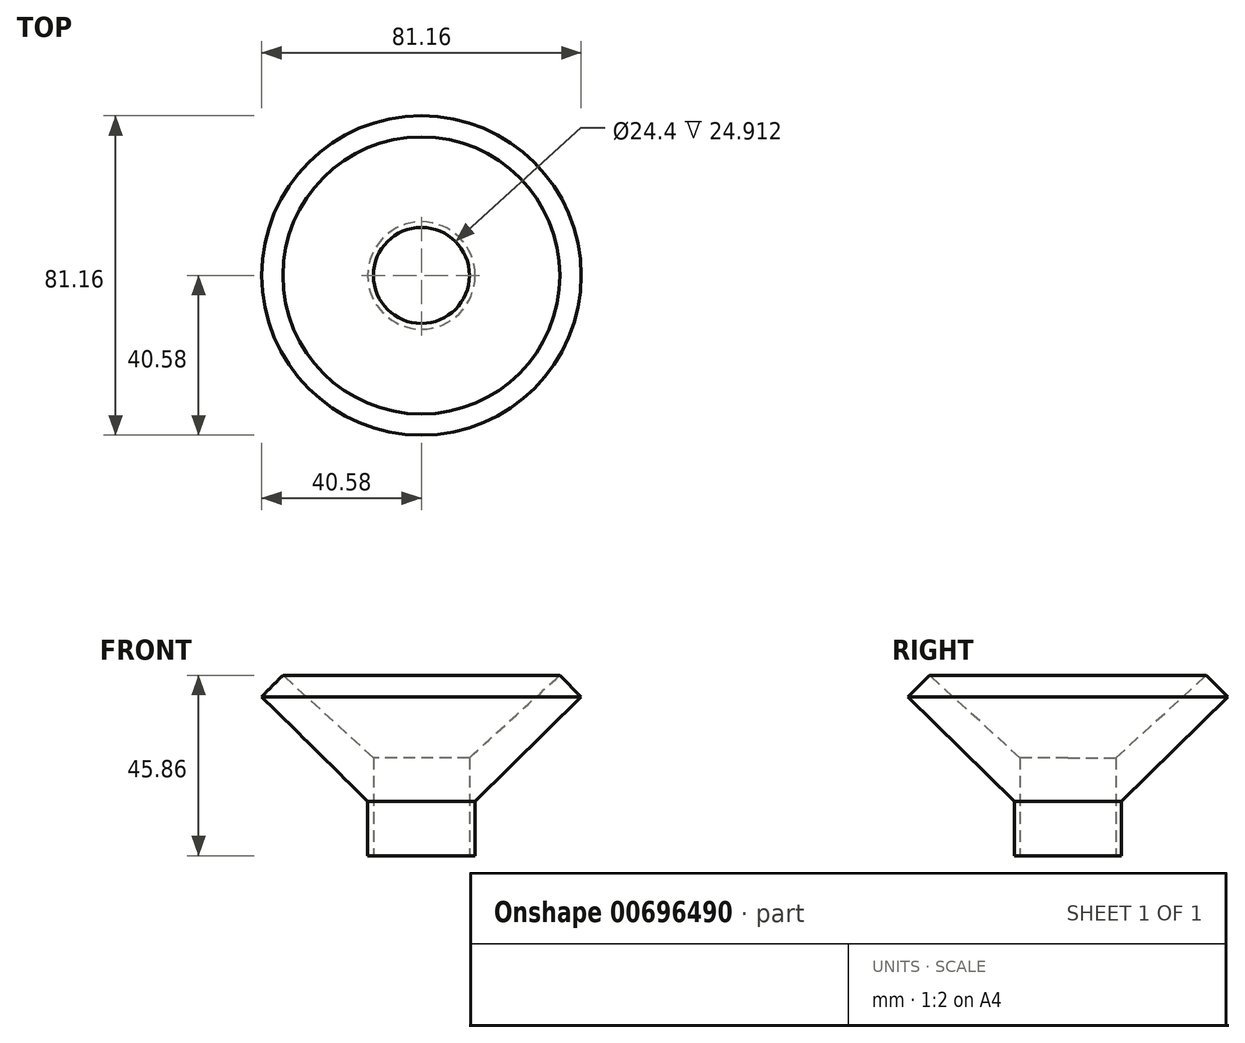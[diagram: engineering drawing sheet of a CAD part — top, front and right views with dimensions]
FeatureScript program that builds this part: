
annotation { "Feature Type Name" : "Feature", "Feature Type Description" : "" }
export const myFeature = defineFeature(function(context is Context, id is Id, definition is map)
    precondition{}
    {
        {
            var Q0;
            Q0=qCreatedBy(makeId("Front.planeOp"),FACE);
            var sketch = newSketch(context, id + "F0", { "sketchPlane" : qUnion([Q0])});
            skLineSegment(sketch, "E0.bottom", {"start": v(0, 0) * mm, "end": v(13.64, 0) * mm});
            skLineSegment(sketch, "E0.top", {"start": v(0, 13.8) * mm, "end": v(13.64, 13.8) * mm});
            skLineSegment(sketch, "E0.left", {"start": v(0, 0) * mm, "end": v(0, 13.8) * mm});
            skLineSegment(sketch, "E0.right", {"start": v(13.64, 0) * mm, "end": v(13.64, 13.8) * mm});
            skLineSegment(sketch, "E1", {"start": v(13.64, 13.8) * mm, "end": v(40.58, 40.42) * mm});
            skLineSegment(sketch, "E2", {"start": v(40.58, 40.42) * mm, "end": v(35.2, 45.86) * mm});
            skLineSegment(sketch, "E3", {"start": v(35.2, 45.86) * mm, "end": v(0, 13.8) * mm});
            skSolve(sketch);
        }
        {
            var Q0;
            Q0 = qSketchRegion(id + "F0", true);
            var Q1;
            Q1=sQuery(id+"F0.wireOp",EDGE,"E0.left");
            revolve(context, id + "F1", {"surfaceOperationType" : NewSurfaceOperationType.NEW, "entities" : qUnion([Q0]), "axis" : qUnion([Q1]), "revolveType" : RevolveType.FULL});
        }
        {
            var Q0;
            Q0=makeQuery(id+"F1.opRevolve","SWEPT_FACE",FACE,{"disambiguationData":[OSD([sQuery(id+"F0.wireOp",EDGE,"E0.bottom")])]});
            var sketch = newSketch(context, id + "F2", { "sketchPlane" : qUnion([Q0])});
            skCircle(sketch, "E4", {"center": v(0, 0) * mm, "radius": 12.2 * mm});
            skSolve(sketch);
        }
        {
            var Q0;
            Q0 = qSketchRegion(id + "F2", true);
            extrude(context, id + "F3", {"entities" : qUnion([Q0]), "operationType" : NewBodyOperationType.REMOVE, "oppositeDirection" : true, "depth" : 25.4 * mm, "offsetDistance" : 25.4 * mm});
        }
    });
